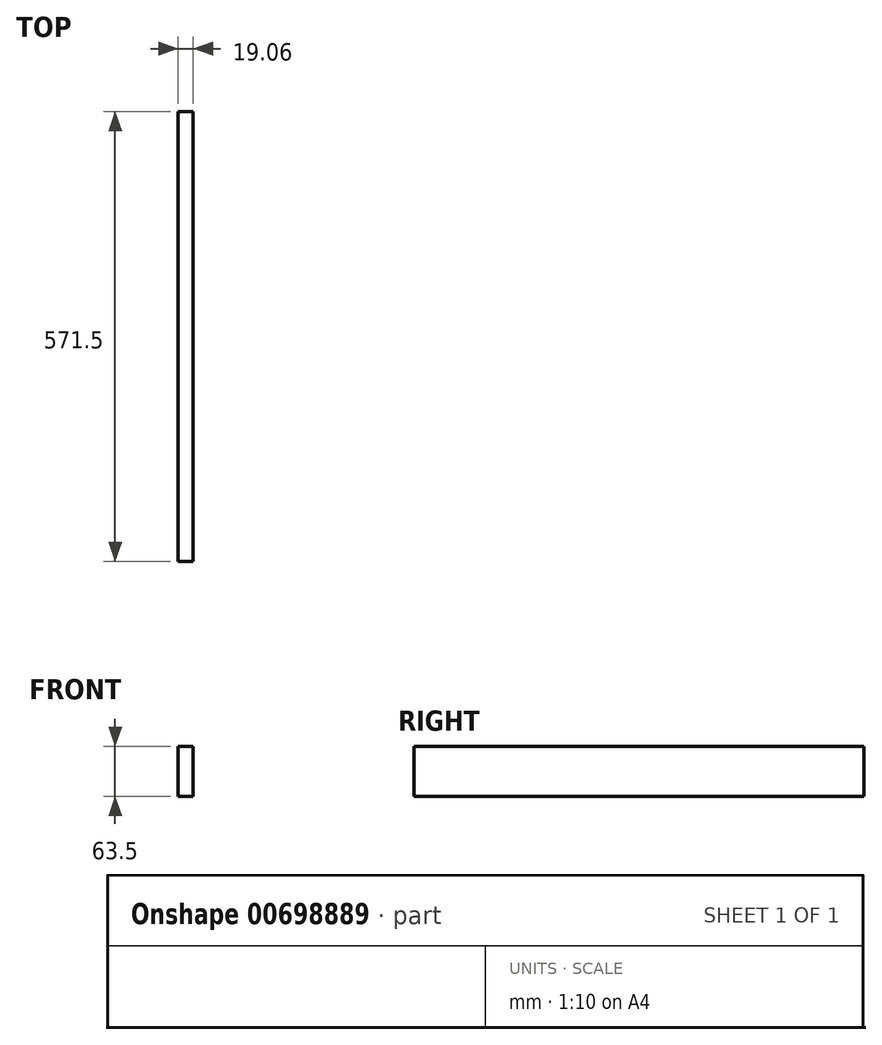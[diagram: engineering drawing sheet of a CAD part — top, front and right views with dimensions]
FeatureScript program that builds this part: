
annotation { "Feature Type Name" : "Feature", "Feature Type Description" : "" }
export const myFeature = defineFeature(function(context is Context, id is Id, definition is map)
    precondition{}
    {
        {
            var Q0;
            Q0=qCreatedBy(makeId("Right.planeOp"),FACE);
            var sketch = newSketch(context, id + "F0", { "sketchPlane" : qUnion([Q0])});
            skLineSegment(sketch, "E0.bottom", {"start": v(285.75, 31.75) * mm, "end": v(-285.75, 31.75) * mm});
            skLineSegment(sketch, "E0.top", {"start": v(285.75, -31.75) * mm, "end": v(-285.75, -31.75) * mm});
            skLineSegment(sketch, "E0.left", {"start": v(285.75, 31.75) * mm, "end": v(285.75, -31.75) * mm});
            skLineSegment(sketch, "E0.right", {"start": v(-285.75, 31.75) * mm, "end": v(-285.75, -31.75) * mm});
            skPoint(sketch, "E0.middle", {"position": v(0, 0) * mm});
            skSolve(sketch);
        }
        {
            var Q0;
            Q0=qSketchRegion(id+"F0",true);
            extrude(context, id + "F1", {"entities" : qUnion([Q0]), "endBound" : BoundingType.SYMMETRIC, "depth" : 19.05 * mm, "offsetDistance" : 25.4 * mm});
        }
    });
